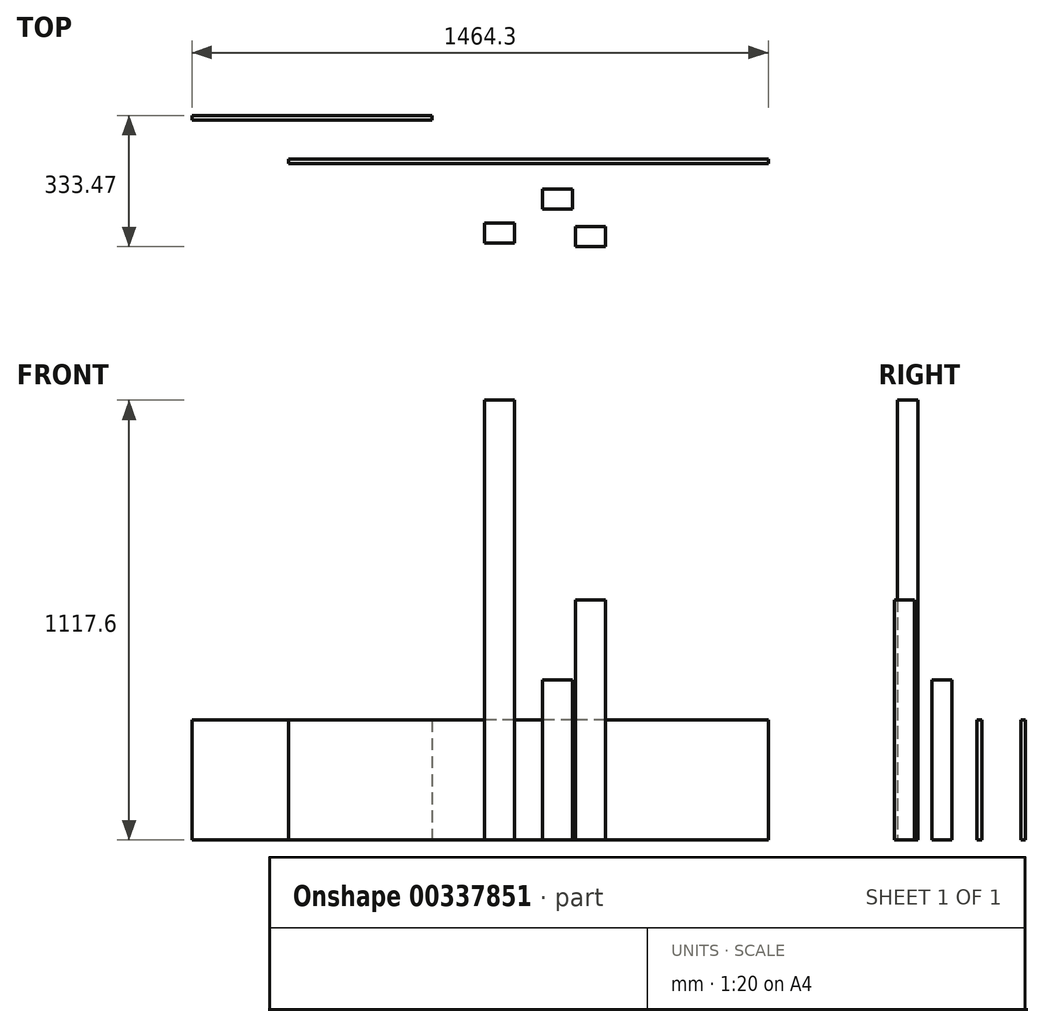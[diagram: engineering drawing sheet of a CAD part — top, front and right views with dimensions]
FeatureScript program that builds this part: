
annotation { "Feature Type Name" : "Feature", "Feature Type Description" : "" }
export const myFeature = defineFeature(function(context is Context, id is Id, definition is map)
    precondition{}
    {
        {
            var Q0;
            Q0=qCreatedBy(makeId("Top.planeOp"),FACE);
            var sketch = newSketch(context, id + "F0", { "sketchPlane" : qUnion([Q0])});
            skLineSegment(sketch, "E0.bottom", {"start": v(38.1, -25.4) * mm, "end": v(-38.1, -25.4) * mm});
            skLineSegment(sketch, "E0.top", {"start": v(38.1, 25.4) * mm, "end": v(-38.1, 25.4) * mm});
            skLineSegment(sketch, "E0.left", {"start": v(38.1, -25.4) * mm, "end": v(38.1, 25.4) * mm});
            skLineSegment(sketch, "E0.right", {"start": v(-38.1, -25.4) * mm, "end": v(-38.1, 25.4) * mm});
            skPoint(sketch, "E0.middle", {"position": v(0, 0) * mm});
            skLineSegment(sketch, "E1.bottom", {"start": v(121.98, -121.25) * mm, "end": v(45.78, -121.25) * mm});
            skLineSegment(sketch, "E1.top", {"start": v(121.98, -70.45) * mm, "end": v(45.78, -70.45) * mm});
            skLineSegment(sketch, "E1.left", {"start": v(121.98, -121.25) * mm, "end": v(121.98, -70.45) * mm});
            skLineSegment(sketch, "E1.right", {"start": v(45.78, -121.25) * mm, "end": v(45.78, -70.45) * mm});
            skPoint(sketch, "E1.middle", {"position": v(83.88, -95.85) * mm});
            skLineSegment(sketch, "E2.bottom", {"start": v(-109.35, -112.56) * mm, "end": v(-185.55, -112.56) * mm});
            skLineSegment(sketch, "E2.top", {"start": v(-109.35, -61.76) * mm, "end": v(-185.55, -61.76) * mm});
            skLineSegment(sketch, "E2.left", {"start": v(-109.35, -112.56) * mm, "end": v(-109.35, -61.76) * mm});
            skLineSegment(sketch, "E2.right", {"start": v(-185.55, -112.56) * mm, "end": v(-185.55, -61.76) * mm});
            skPoint(sketch, "E2.middle", {"position": v(-147.45, -87.16) * mm});
            skLineSegment(sketch, "E3.bottom", {"start": v(535.41, 89.4) * mm, "end": v(-683.79, 89.4) * mm});
            skLineSegment(sketch, "E3.top", {"start": v(535.41, 101.34) * mm, "end": v(-683.79, 101.34) * mm});
            skLineSegment(sketch, "E3.left", {"start": v(535.41, 89.4) * mm, "end": v(535.41, 101.34) * mm});
            skLineSegment(sketch, "E3.right", {"start": v(-683.79, 89.4) * mm, "end": v(-683.79, 101.34) * mm});
            skPoint(sketch, "E3.middle", {"position": v(-74.19, 95.37) * mm});
            skLineSegment(sketch, "E4.bottom", {"start": v(-319.29, 200.28) * mm, "end": v(-928.89, 200.28) * mm});
            skLineSegment(sketch, "E4.top", {"start": v(-319.29, 212.22) * mm, "end": v(-928.89, 212.22) * mm});
            skLineSegment(sketch, "E4.left", {"start": v(-319.29, 200.28) * mm, "end": v(-319.29, 212.22) * mm});
            skLineSegment(sketch, "E4.right", {"start": v(-928.89, 200.28) * mm, "end": v(-928.89, 212.22) * mm});
            skPoint(sketch, "E4.middle", {"position": v(-624.09, 206.25) * mm});
            skSolve(sketch);
        }
        {
            var Q0;
            Q0=makeQuery(id+"F0.imprint","IMPRINT",FACE,{"disambiguationData":[TD([[makeQuery(id+"F0.imprint","IMPRINT",EDGE,{"derivedFrom":sQuery(id+"F0.wireOp",EDGE,"E0.bottom")}),-1.0]])]});
            extrude(context, id + "F1", {"entities" : qUnion([Q0]), "depth" : 406.4 * mm});
        }
        {
            var Q0;
            Q0=makeQuery(id+"F0.imprint","IMPRINT",FACE,{"disambiguationData":[TD([[makeQuery(id+"F0.imprint","IMPRINT",EDGE,{"derivedFrom":sQuery(id+"F0.wireOp",EDGE,"E1.bottom")}),-1.0]])]});
            extrude(context, id + "F2", {"entities" : qUnion([Q0]), "depth" : 609.6 * mm});
        }
        {
            var Q0;
            Q0=makeQuery(id+"F0.imprint","IMPRINT",FACE,{"disambiguationData":[TD([[makeQuery(id+"F0.imprint","IMPRINT",EDGE,{"derivedFrom":sQuery(id+"F0.wireOp",EDGE,"E2.bottom")}),-1.0]])]});
            extrude(context, id + "F3", {"entities" : qUnion([Q0]), "depth" : 1117.6 * mm});
        }
        {
            var Q0;
            Q0=makeQuery(id+"F0.imprint","IMPRINT",FACE,{"disambiguationData":[TD([[makeQuery(id+"F0.imprint","IMPRINT",EDGE,{"derivedFrom":sQuery(id+"F0.wireOp",EDGE,"E3.bottom")}),-1.0]])]});
            extrude(context, id + "F4", {"entities" : qUnion([Q0]), "depth" : 304.8 * mm});
        }
        {
            var Q0;
            Q0=makeQuery(id+"F0.imprint","IMPRINT",FACE,{"disambiguationData":[TD([[makeQuery(id+"F0.imprint","IMPRINT",EDGE,{"derivedFrom":sQuery(id+"F0.wireOp",EDGE,"E4.bottom")}),-1.0]])]});
            extrude(context, id + "F5", {"entities" : qUnion([Q0]), "depth" : 304.8 * mm});
        }
    });
